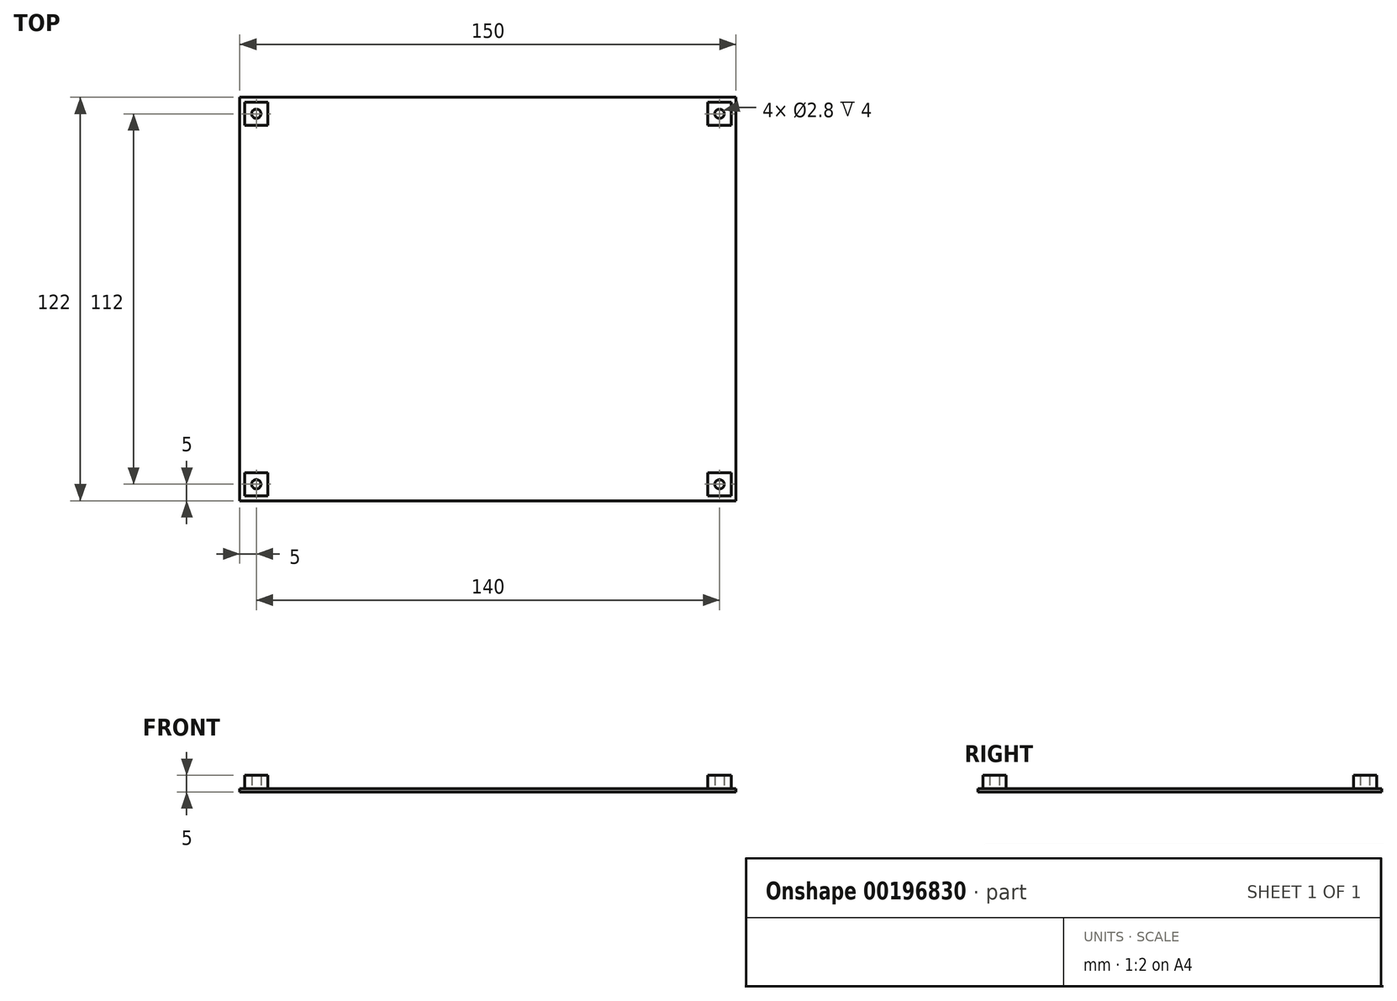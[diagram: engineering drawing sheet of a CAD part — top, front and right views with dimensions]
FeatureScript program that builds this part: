
annotation { "Feature Type Name" : "Feature", "Feature Type Description" : "" }
export const myFeature = defineFeature(function(context is Context, id is Id, definition is map)
    precondition{}
    {
        {
            var Q0;
            Q0=qCreatedBy(makeId("Top.planeOp"),FACE);
            var sketch = newSketch(context, id + "F0", { "sketchPlane" : qUnion([Q0])});
            skLineSegment(sketch, "E0.bottom", {"start": v(75, -61) * mm, "end": v(-75, -61) * mm});
            skLineSegment(sketch, "E0.top", {"start": v(75, 61) * mm, "end": v(-75, 61) * mm});
            skLineSegment(sketch, "E0.left", {"start": v(75, -61) * mm, "end": v(75, 61) * mm});
            skLineSegment(sketch, "E0.right", {"start": v(-75, -61) * mm, "end": v(-75, 61) * mm});
            skPoint(sketch, "E0.middle", {"position": v(0, 0) * mm});
            skSolve(sketch);
        }
        {
            var Q0;
            Q0=qSketchRegion(id+"F0",true);
            extrude(context, id + "F1", {"entities" : qUnion([Q0]), "depth" : 1 * mm});
        }
        {
            var Q0;
            Q0=makeQuery(id+"F1.opExtrude","CAP_FACE",FACE,{"disambiguationData":[OSD([sQuery(id+"F0.wireOp",EDGE,"E0.bottom"),sQuery(id+"F0.wireOp",EDGE,"E0.top"),sQuery(id+"F0.wireOp",EDGE,"E0.left"),sQuery(id+"F0.wireOp",EDGE,"E0.right")])],"isStart":false});
            var sketch = newSketch(context, id + "F2", { "sketchPlane" : qUnion([Q0])});
            skLineSegment(sketch, "E1.bottom", {"start": v(-66.5, 52.5) * mm, "end": v(-73.5, 52.5) * mm});
            skLineSegment(sketch, "E1.top", {"start": v(-66.5, 59.5) * mm, "end": v(-73.5, 59.5) * mm});
            skLineSegment(sketch, "E1.left", {"start": v(-66.5, 52.5) * mm, "end": v(-66.5, 59.5) * mm});
            skLineSegment(sketch, "E1.right", {"start": v(-73.5, 52.5) * mm, "end": v(-73.5, 59.5) * mm});
            skPoint(sketch, "E1.middle", {"position": v(-70, 56) * mm});
            skLineSegment(sketch, "E2.bottom", {"start": v(73.5, 52.5) * mm, "end": v(66.5, 52.5) * mm});
            skLineSegment(sketch, "E2.top", {"start": v(73.5, 59.5) * mm, "end": v(66.5, 59.5) * mm});
            skLineSegment(sketch, "E2.left", {"start": v(73.5, 52.5) * mm, "end": v(73.5, 59.5) * mm});
            skLineSegment(sketch, "E2.right", {"start": v(66.5, 52.5) * mm, "end": v(66.5, 59.5) * mm});
            skPoint(sketch, "E2.middle", {"position": v(70, 56) * mm});
            skPoint(sketch, "E2.middle.positionSnap0", {"position": v(-66.5, 56) * mm});
            skPoint(sketch, "E2.centerSnap0", {"position": v(-66.5, 56) * mm});
            skLineSegment(sketch, "E3.bottom", {"start": v(-66.5, -59.5) * mm, "end": v(-73.5, -59.5) * mm});
            skLineSegment(sketch, "E3.top", {"start": v(-66.5, -52.5) * mm, "end": v(-73.5, -52.5) * mm});
            skLineSegment(sketch, "E3.left", {"start": v(-66.5, -59.5) * mm, "end": v(-66.5, -52.5) * mm});
            skLineSegment(sketch, "E3.right", {"start": v(-73.5, -59.5) * mm, "end": v(-73.5, -52.5) * mm});
            skPoint(sketch, "E3.middle", {"position": v(-70, -56) * mm});
            skLineSegment(sketch, "E4.bottom", {"start": v(73.5, -59.5) * mm, "end": v(66.5, -59.5) * mm});
            skLineSegment(sketch, "E4.top", {"start": v(73.5, -52.5) * mm, "end": v(66.5, -52.5) * mm});
            skLineSegment(sketch, "E4.left", {"start": v(73.5, -59.5) * mm, "end": v(73.5, -52.5) * mm});
            skLineSegment(sketch, "E4.right", {"start": v(66.5, -59.5) * mm, "end": v(66.5, -52.5) * mm});
            skPoint(sketch, "E4.middle", {"position": v(70, -56) * mm});
            skPoint(sketch, "E4.middle.positionSnap0", {"position": v(-66.5, -56) * mm});
            skPoint(sketch, "E4.centerSnap0", {"position": v(-66.5, -56) * mm});
            skCircle(sketch, "E5", {"center": v(-70, 56) * mm, "radius": 1.4 * mm});
            skCircle(sketch, "E6", {"center": v(70, 56) * mm, "radius": 1.4 * mm});
            skCircle(sketch, "E7", {"center": v(70, -56) * mm, "radius": 1.4 * mm});
            skCircle(sketch, "E8", {"center": v(-70, -56) * mm, "radius": 1.4 * mm});
            skSolve(sketch);
        }
        {
            var Q0;
            Q0=qSketchRegion(id+"F2",true);
            extrude(context, id + "F3", {"entities" : qUnion([Q0]), "operationType" : NewBodyOperationType.ADD, "depth" : 4 * mm});
        }
    });
